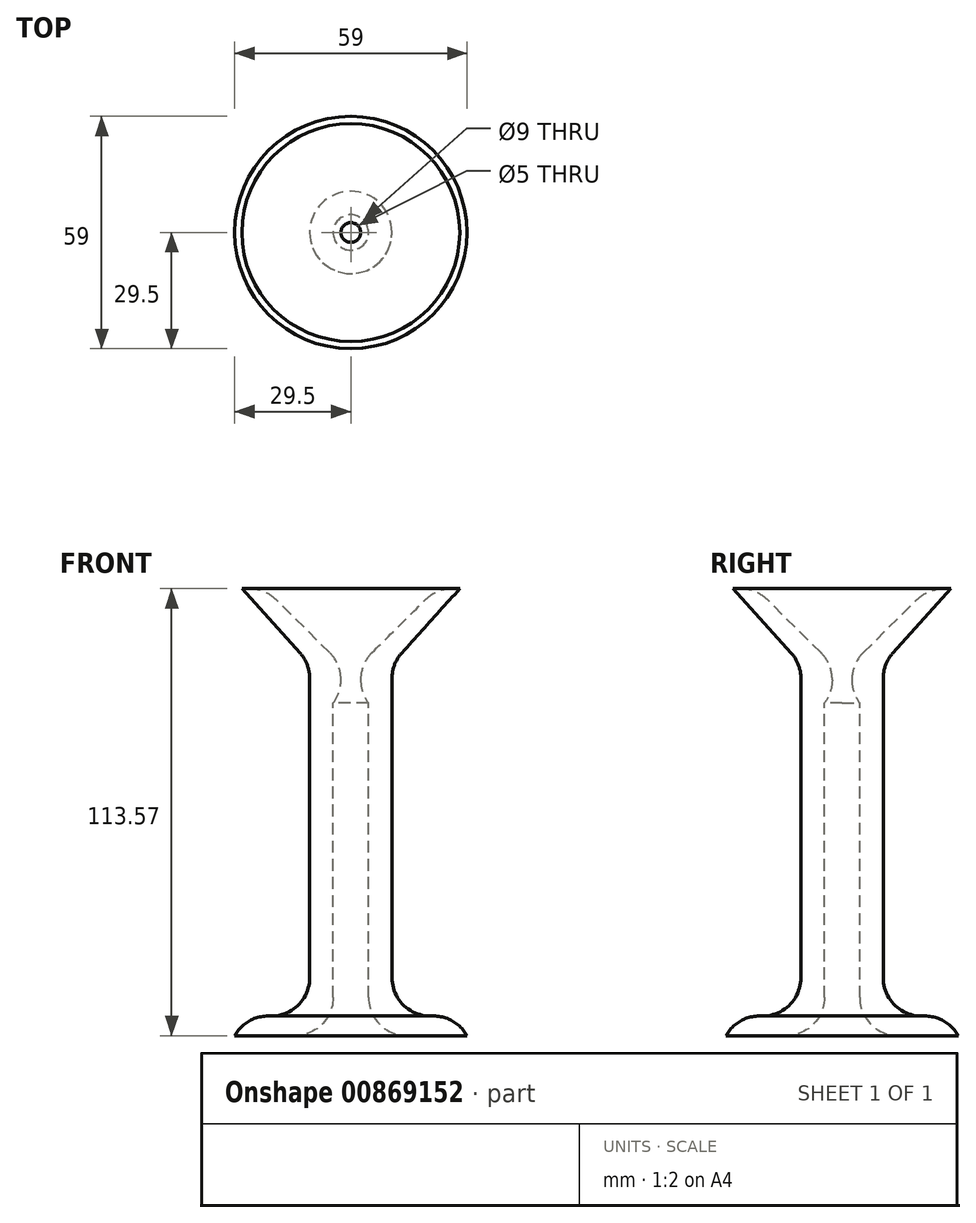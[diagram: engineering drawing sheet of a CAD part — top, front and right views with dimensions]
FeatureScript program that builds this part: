
annotation { "Feature Type Name" : "Feature", "Feature Type Description" : "" }
export const myFeature = defineFeature(function(context is Context, id is Id, definition is map)
    precondition{}
    {
        {
            var Q0;
            Q0=qCreatedBy(makeId("Front.planeOp"),FACE);
            var sketch = newSketch(context, id + "F0", { "sketchPlane" : qUnion([Q0])});
            skLineSegment(sketch, "E0", {"start": v(0, 129.92) * mm, "end": v(0, -128.67) * mm, "construction": true});
            skLineSegment(sketch, "E1", {"start": v(4.5, 0) * mm, "end": v(29.5, 0) * mm});
            skLineSegment(sketch, "E2", {"start": v(29.5, 0) * mm, "end": v(29.5, 5) * mm});
            skLineSegment(sketch, "E3", {"start": v(29.5, 5) * mm, "end": v(10.46, 5) * mm});
            skLineSegment(sketch, "E4", {"start": v(10.46, 5) * mm, "end": v(10.46, 94.5) * mm});
            skLineSegment(sketch, "E5", {"start": v(27.69, 113.57) * mm, "end": v(10.46, 94.5) * mm});
            skPoint(sketch, "E6.start.orphan", {"position": v(0, 5) * mm});
            skLineSegment(sketch, "E7", {"start": v(4.5, 84.5) * mm, "end": v(4.5, 0) * mm});
            skLineSegment(sketch, "E8.top", {"start": v(4.5, 84.5) * mm, "end": v(2.5, 84.5) * mm});
            skLineSegment(sketch, "E8.right", {"start": v(2.5, 94.5) * mm, "end": v(2.5, 84.5) * mm});
            skLineSegment(sketch, "E9", {"start": v(2.5, 94.5) * mm, "end": v(21.85, 113.57) * mm});
            skLineSegment(sketch, "E10", {"start": v(21.85, 113.57) * mm, "end": v(27.69, 113.57) * mm});
            skSolve(sketch);
        }
        {
            var Q0;
            Q0=makeQuery(id+"F0.imprint","IMPRINT",FACE,{"disambiguationData":[TD([[makeQuery(id+"F0.imprint","IMPRINT",EDGE,{"derivedFrom":sQuery(id+"F0.wireOp",EDGE,"E1")}),1.0]])]});
            var Q1;
            Q1=sQuery(id+"F0.wireOp",EDGE,"E0");
            revolve(context, id + "F1", {"surfaceOperationType" : NewSurfaceOperationType.NEW, "entities" : qUnion([Q0]), "axis" : qUnion([Q1]), "revolveType" : RevolveType.FULL});
        }
        {
            var Q0;
            Q0=makeQuery(id+"F1.opRevolve","SWEPT_FACE",FACE,{"disambiguationData":[OSD([sQuery(id+"F0.wireOp",EDGE,"E9")])]});
            var Q1;
            Q1=makeQuery(id+"F1.opRevolve","SWEPT_EDGE",EDGE,{"disambiguationData":[OSD([sQuery(id+"F0.wireOp",EDGE,"E8.top"),sQuery(id+"F0.wireOp",EDGE,"E8.right")])]});
            var Q2;
            Q2=makeQuery(id+"F1.opRevolve","SWEPT_EDGE",EDGE,{"disambiguationData":[OSD([sQuery(id+"F0.wireOp",EDGE,"E1"),sQuery(id+"F0.wireOp",EDGE,"E7")])]});
            var Q3;
            Q3=makeQuery(id+"F1.opRevolve","SWEPT_FACE",FACE,{"disambiguationData":[OSD([sQuery(id+"F0.wireOp",EDGE,"E3")])]});
            var Q4;
            Q4=makeQuery(id+"F1.opRevolve","SWEPT_EDGE",EDGE,{"disambiguationData":[OSD([sQuery(id+"F0.wireOp",EDGE,"E4"),sQuery(id+"F0.wireOp",EDGE,"E5")])]});
            fillet(context, id + "F2", {"entities" : qUnion([Q0, Q1, Q2, Q3, Q4]), "radius" : 9.7 * mm, "tangentPropagation" : true, "allowEdgeOverflow" : false});
        }
    });
